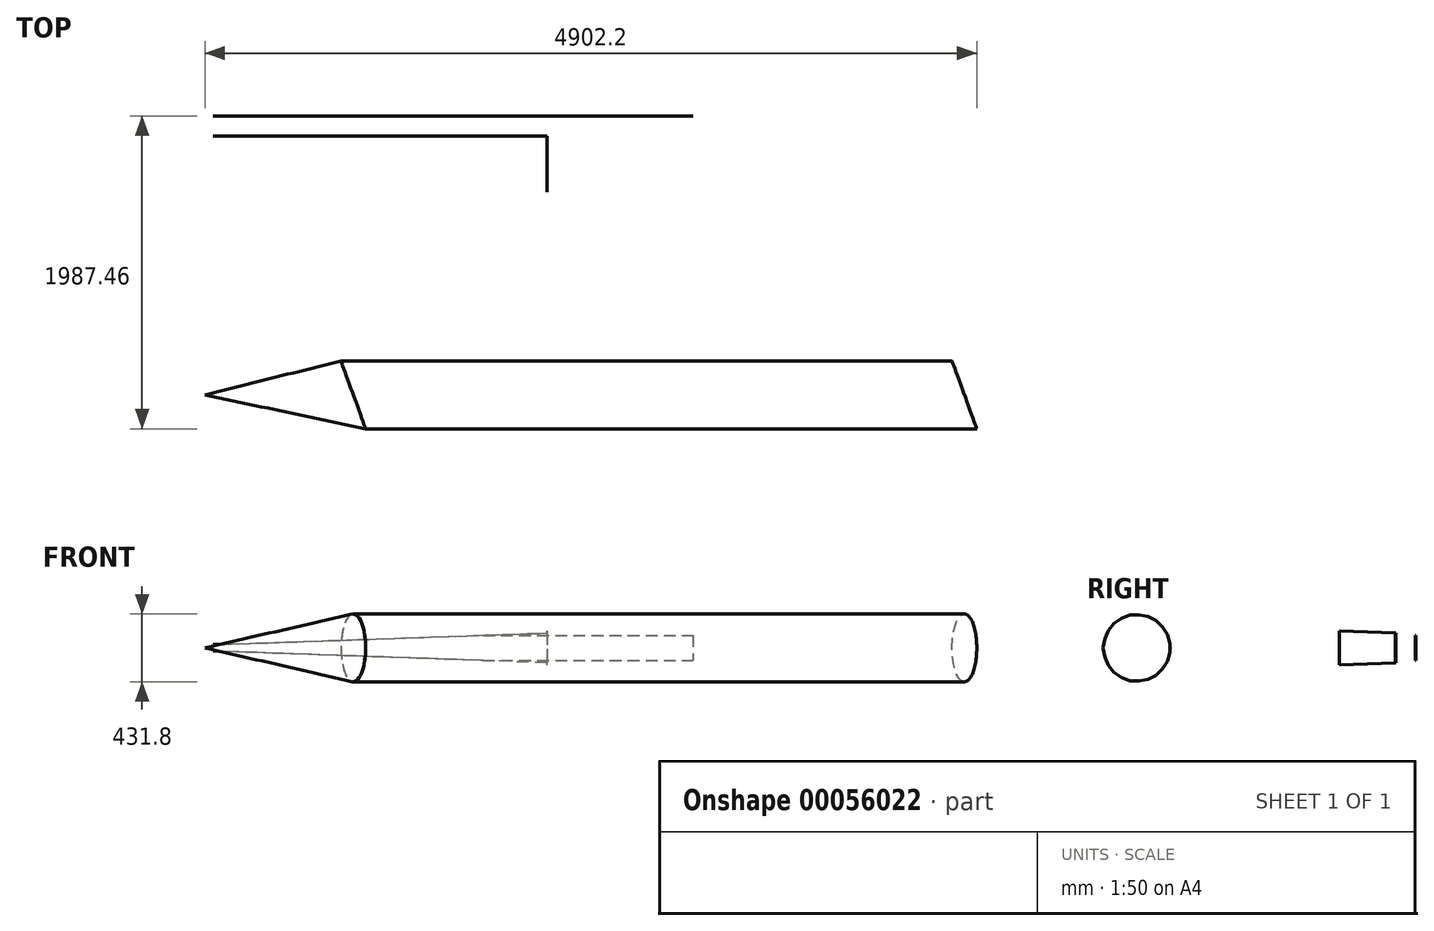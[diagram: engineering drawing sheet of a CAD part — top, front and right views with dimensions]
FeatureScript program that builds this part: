
annotation { "Feature Type Name" : "Feature", "Feature Type Description" : "" }
export const myFeature = defineFeature(function(context is Context, id is Id, definition is map)
    precondition{}
    {
        {
            var Q0;
            Q0=qCreatedBy(makeId("Front.planeOp"),FACE);
            var sketch = newSketch(context, id + "F0", { "sketchPlane" : qUnion([Q0])});
            skLineSegment(sketch, "E0", {"start": v(-812.8, 20.56) * mm, "end": v(2235.2, 127) * mm});
            skLineSegment(sketch, "E1", {"start": v(2235.2, 127) * mm, "end": v(2235.2, -127) * mm});
            skLineSegment(sketch, "E2", {"start": v(2235.2, -127) * mm, "end": v(-812.8, -20.56) * mm});
            skLineSegment(sketch, "E3", {"start": v(-812.8, -20.56) * mm, "end": v(-812.8, 20.56) * mm});
            skLineSegment(sketch, "E4", {"start": v(1307.81, 94.62) * mm, "end": v(1307.81, -94.61) * mm});
            skLineSegment(sketch, "E5", {"start": v(1663.41, 107.03) * mm, "end": v(1663.41, -107.03) * mm});
            skLineSegment(sketch, "E6", {"start": v(901.41, 80.42) * mm, "end": v(901.41, -80.42) * mm});
            skLineSegment(sketch, "E7", {"start": v(901.41, 80.42) * mm, "end": v(2235.2, 80.42) * mm});
            skLineSegment(sketch, "E8", {"start": v(901.41, -80.42) * mm, "end": v(2235.2, -80.42) * mm});
            skSolve(sketch);
        }
        {
            var Q0;
            {var subQ0=sQuery(id+"F0.wireOp",EDGE,"E3");Q0=makeQuery(id+"F0.imprint","IMPRINT",FACE,{"disambiguationData":[TD([[makeQuery(id+"F0.imprint","IMPRINT",EDGE,{"derivedFrom":subQ0}),-1.0]])]});}
            var Q1;
            {var subQ5=sQuery(id+"F0.wireOp",EDGE,"E6");Q1=makeQuery(id+"F0.imprint","IMPRINT",FACE,{"disambiguationData":[TD([[makeQuery(id+"F0.imprint","IMPRINT",EDGE,{"derivedFrom":subQ5}),1.0]])]});}
            var Q2;
            {var subQ0=sQuery(id+"F0.wireOp",EDGE,"E7");var subQ1=sQuery(id+"F0.wireOp",EDGE,"E4");var subQ2=makeQuery(id+"F0.imprint","INTERSECT",VERTEX,{"derivedFrom":[subQ1,subQ0]});Q2=makeQuery(id+"F0.imprint","IMPRINT",FACE,{"disambiguationData":[TD([[makeQuery(id+"F0.imprint","IMPRINT",EDGE,{"disambiguationData":[TD([[subQ2,-1.0]])],"derivedFrom":subQ1}),1.0]])]});}
            var Q3;
            {var subQ0=sQuery(id+"F0.wireOp",EDGE,"E7");var subQ1=sQuery(id+"F0.wireOp",EDGE,"E1");var subQ2=makeQuery(id+"F0.imprint","INTERSECT",VERTEX,{"derivedFrom":[subQ1,subQ0]});Q3=makeQuery(id+"F0.imprint","IMPRINT",FACE,{"disambiguationData":[TD([[makeQuery(id+"F0.imprint","IMPRINT",EDGE,{"disambiguationData":[TD([[subQ2,-1.0]])],"derivedFrom":subQ1}),-1.0]])]});}
            extrude(context, id + "F1", {"entities" : qUnion([Q0, Q1, Q2, Q3]), "depth" : 1.02 * mm, "offsetDistance" : 25.4 * mm, "symmetric" : true});
        }
        {
            var Q0;
            {var subQ0=sQuery(id+"F0.wireOp",EDGE,"E4");var subQ1=sQuery(id+"F0.wireOp",EDGE,"E2");var subQ2=makeQuery(id+"F0.imprint","INTERSECT",VERTEX,{"derivedFrom":[subQ1,subQ0]});Q0=makeQuery(id+"F0.imprint","IMPRINT",FACE,{"disambiguationData":[TD([[makeQuery(id+"F0.imprint","IMPRINT",EDGE,{"disambiguationData":[TD([[subQ2,1.0]])],"derivedFrom":subQ0}),-1.0]])]});}
            var Q1;
            {var subQ0=sQuery(id+"F0.wireOp",EDGE,"E4");var subQ1=sQuery(id+"F0.wireOp",EDGE,"E0");var subQ2=makeQuery(id+"F0.imprint","INTERSECT",VERTEX,{"derivedFrom":[subQ1,subQ0]});Q1=makeQuery(id+"F0.imprint","IMPRINT",FACE,{"disambiguationData":[TD([[makeQuery(id+"F0.imprint","IMPRINT",EDGE,{"disambiguationData":[TD([[subQ2,-1.0]])],"derivedFrom":subQ0}),-1.0]])]});}
            var Q2;
            {var subQ5=sQuery(id+"F0.wireOp",EDGE,"E6");Q2=makeQuery(id+"F0.imprint","IMPRINT",FACE,{"disambiguationData":[TD([[makeQuery(id+"F0.imprint","IMPRINT",EDGE,{"derivedFrom":subQ5}),1.0]])]});}
            var Q3;
            {var subQ0=sQuery(id+"F0.wireOp",EDGE,"E3");Q3=makeQuery(id+"F0.imprint","IMPRINT",FACE,{"disambiguationData":[TD([[makeQuery(id+"F0.imprint","IMPRINT",EDGE,{"derivedFrom":subQ0}),-1.0]])]});}
            extrude(context, id + "F2", {"entities" : qUnion([Q0, Q1, Q2, Q3]), "depth" : 128.02 * mm, "offsetDistance" : 25.4 * mm, "hasSecondDirection" : true, "secondDirectionOppositeDirection" : false, "secondDirectionDepth" : 127 * mm});
        }
        {
            var Q0;
            {var subQ0=sQuery(id+"F0.wireOp",EDGE,"E4");Q0=makeQuery(id+"F0.imprint","IMPRINT",FACE,{"disambiguationData":[TD([[makeQuery(id+"F0.imprint","IMPRINT",EDGE,{"derivedFrom":subQ0}),1.0]])]});}
            extrude(context, id + "F3", {"entities" : qUnion([Q0]), "depth" : 128.02 * mm, "offsetDistance" : 25.4 * mm, "hasSecondDirection" : true, "secondDirectionOppositeDirection" : false, "secondDirectionDepth" : 127 * mm});
        }
        {
            var Q0;
            Q0=makeQuery(id+"F3.opExtrude","SWEPT_BODY",BODY,{"disambiguationData":[OSD([sQuery(id+"F0.wireOp",EDGE,"E0"),sQuery(id+"F0.wireOp",EDGE,"E1"),sQuery(id+"F0.wireOp",EDGE,"E2"),sQuery(id+"F0.wireOp",EDGE,"E4")])]});
            var Q1;
            Q1=makeQuery(id+"F2.opExtrude","CAP_EDGE",EDGE,{"disambiguationData":[OSD([sQuery(id+"F0.wireOp",EDGE,"E4")])],"isStart":false});
            transform(context, id + "F4", {"entities" : qUnion([Q0]), "transformType" : TransformType.ROTATION, "transformAxis" : qUnion([Q1]), "angle" : 90 * degree, "makeCopy" : false});
        }
        {
            var Q0;
            Q0=qCreatedBy(makeId("Top.planeOp"),FACE);
            var sketch = newSketch(context, id + "F5", { "sketchPlane" : qUnion([Q0])});
            skLineSegment(sketch, "E9", {"start": v(0, -1771.05) * mm, "end": v(0, -1555.15) * mm});
            skLineSegment(sketch, "E10", {"start": v(0, -1555.15) * mm, "end": v(4038.6, -1555.15) * mm});
            skLineSegment(sketch, "E11", {"start": v(4038.6, -1555.15) * mm, "end": v(4038.6, -1771.05) * mm});
            skLineSegment(sketch, "E12", {"start": v(4038.6, -1771.05) * mm, "end": v(0, -1771.05) * mm});
            skLineSegment(sketch, "E13", {"start": v(0, -1555.15) * mm, "end": v(-863.6, -1771.05) * mm});
            skLineSegment(sketch, "E14", {"start": v(-863.6, -1771.05) * mm, "end": v(0, -1771.05) * mm});
            skLineSegment(sketch, "E15", {"start": v(0, -1555.15) * mm, "end": v(0, -1986.95) * mm});
            skLineSegment(sketch, "E16", {"start": v(0, -1986.95) * mm, "end": v(157.16, -1986.95) * mm});
            skLineSegment(sketch, "E17", {"start": v(157.16, -1986.95) * mm, "end": v(0, -1555.15) * mm});
            skLineSegment(sketch, "E18", {"start": v(4038.6, -1986.95) * mm, "end": v(4038.6, -1555.15) * mm});
            skLineSegment(sketch, "E19", {"start": v(3881.44, -1555.15) * mm, "end": v(4038.6, -1986.95) * mm});
            skSolve(sketch);
        }
        {
            var Q0;
            {var subQ3=sQuery(id+"F5.wireOp",EDGE,"E19");var subQ5=sQuery(id+"F5.wireOp",EDGE,"E12");var subQ7=makeQuery(id+"F5.imprint","INTERSECT",VERTEX,{"derivedFrom":[subQ5,subQ3]});Q0=makeQuery(id+"F5.imprint","IMPRINT",FACE,{"disambiguationData":[TD([[makeQuery(id+"F5.imprint","IMPRINT",EDGE,{"disambiguationData":[TD([[subQ7,-1.0]])],"derivedFrom":subQ5}),-1.0]])]});}
            var Q1;
            {var subQ0=sQuery(id+"F5.wireOp",EDGE,"E11");Q1=makeQuery(id+"F5.imprint","IMPRINT",FACE,{"disambiguationData":[TD([[makeQuery(id+"F5.imprint","IMPRINT",EDGE,{"derivedFrom":subQ0}),-1.0]])]});}
            var Q2;
            {var subQ0=sQuery(id+"F5.wireOp",EDGE,"E9");Q2=makeQuery(id+"F5.imprint","IMPRINT",FACE,{"disambiguationData":[TD([[makeQuery(id+"F5.imprint","IMPRINT",EDGE,{"derivedFrom":subQ0}),-1.0]])]});}
            var Q3;
            Q3=sQuery(id+"F5.wireOp",EDGE,"E12");
            revolve(context, id + "F6", {"surfaceOperationType" : NewSurfaceOperationType.NEW, "entities" : qUnion([Q0, Q1, Q2]), "axis" : qUnion([Q3]), "revolveType" : RevolveType.FULL});
        }
        {
            var Q0;
            {var subQ0=sQuery(id+"F5.wireOp",EDGE,"E15");Q0=makeQuery(id+"F5.imprint","IMPRINT",FACE,{"disambiguationData":[TD([[makeQuery(id+"F5.imprint","IMPRINT",EDGE,{"derivedFrom":subQ0}),1.0]])]});}
            var Q1;
            {var subQ0=sQuery(id+"F5.wireOp",EDGE,"E9");Q1=makeQuery(id+"F5.imprint","IMPRINT",FACE,{"disambiguationData":[TD([[makeQuery(id+"F5.imprint","IMPRINT",EDGE,{"derivedFrom":subQ0}),-1.0]])]});}
            var Q2;
            {var subQ0=sQuery(id+"F5.wireOp",EDGE,"E11");Q2=makeQuery(id+"F5.imprint","IMPRINT",FACE,{"disambiguationData":[TD([[makeQuery(id+"F5.imprint","IMPRINT",EDGE,{"derivedFrom":subQ0}),-1.0]])]});}
            var Q3;
            {var subQ0=sQuery(id+"F5.wireOp",EDGE,"E18");Q3=makeQuery(id+"F5.imprint","IMPRINT",FACE,{"disambiguationData":[TD([[makeQuery(id+"F5.imprint","IMPRINT",EDGE,{"derivedFrom":subQ0}),1.0]])]});}
            var Q4;
            {var subQ0=sQuery(id+"F5.wireOp",EDGE,"E15");Q4=makeQuery(id+"F5.imprint","IMPRINT",FACE,{"disambiguationData":[TD([[makeQuery(id+"F5.imprint","IMPRINT",EDGE,{"derivedFrom":subQ0}),1.0]])]});}
            extrude(context, id + "F7", {"entities" : qUnion([Q0, Q1, Q2, Q3, Q4]), "operationType" : NewBodyOperationType.REMOVE, "depth" : 508 * mm, "offsetDistance" : 25.4 * mm, "symmetric" : true});
        }
        {
            var Q0;
            Q0=makeQuery(id+"F7.boolean.opBoolean","COPY",FACE,{"derivedFrom":makeQuery(id+"F7.opExtrude","SWEPT_FACE",FACE,{"disambiguationData":[OSD([sQuery(id+"F5.wireOp",EDGE,"E17")])]})});
            var Q1;
            Q1=sQuery(id+"F5.wireOp",VERTEX,"E13.end");
            var Q2;
            Q2=makeQuery(id+"F7.boolean.opBoolean","INTERSECT",EDGE,{"derivedFrom":[makeQuery(id+"F6.opRevolve","SWEPT_FACE",FACE,{"disambiguationData":[OSD([sQuery(id+"F5.wireOp",EDGE,"E10")])]}),makeQuery(id+"F7.opExtrude","SWEPT_FACE",FACE,{"disambiguationData":[OSD([sQuery(id+"F5.wireOp",EDGE,"E17")])]})]});
            var Q3;
            Q3=sQuery(id+"F5.wireOp",VERTEX,"E13.end");
            loft(context, id + "F8", {"sheetProfilesArray" : [{ "sheetProfileEntities" : qUnion([Q0]) }, { "sheetProfileEntities" : qUnion([Q1]) }], "wireProfilesArray" : [{ "wireProfileEntities" : qUnion([Q2]) }, { "wireProfileEntities" : qUnion([Q3]) }]});
        }
    });
